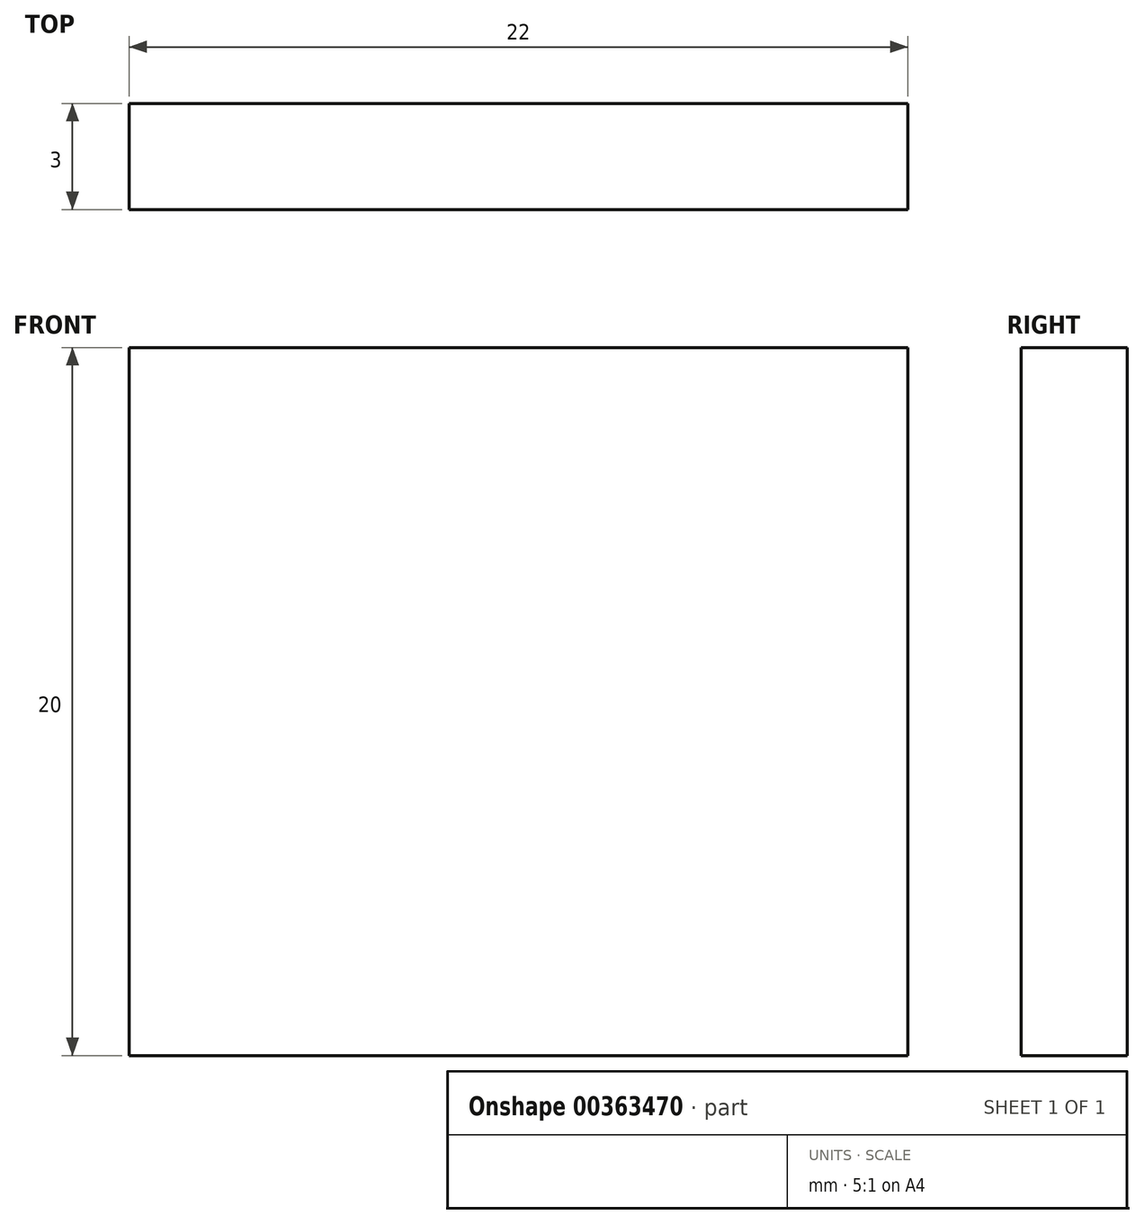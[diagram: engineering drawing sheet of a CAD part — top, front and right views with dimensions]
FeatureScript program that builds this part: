
annotation { "Feature Type Name" : "Feature", "Feature Type Description" : "" }
export const myFeature = defineFeature(function(context is Context, id is Id, definition is map)
    precondition{}
    {
        {
            var Q0;
            Q0=qCreatedBy(makeId("Front.planeOp"),FACE);
            var sketch = newSketch(context, id + "F0", { "sketchPlane" : qUnion([Q0])});
            skLineSegment(sketch, "E0.bottom", {"start": v(0, 0) * mm, "end": v(22, 0) * mm});
            skLineSegment(sketch, "E0.top", {"start": v(0, 20) * mm, "end": v(22, 20) * mm});
            skLineSegment(sketch, "E0.left", {"start": v(0, 0) * mm, "end": v(0, 20) * mm});
            skLineSegment(sketch, "E0.right", {"start": v(22, 0) * mm, "end": v(22, 20) * mm});
            skSolve(sketch);
        }
        {
            var Q0;
            Q0=makeQuery(id+"F0.imprint","IMPRINT",FACE,{"disambiguationData":[TD([[makeQuery(id+"F0.imprint","IMPRINT",EDGE,{"derivedFrom":sQuery(id+"F0.wireOp",EDGE,"E0.bottom")}),1.0]])]});
            extrude(context, id + "F1", {"entities" : qUnion([Q0]), "depth" : 3 * mm});
        }
    });
